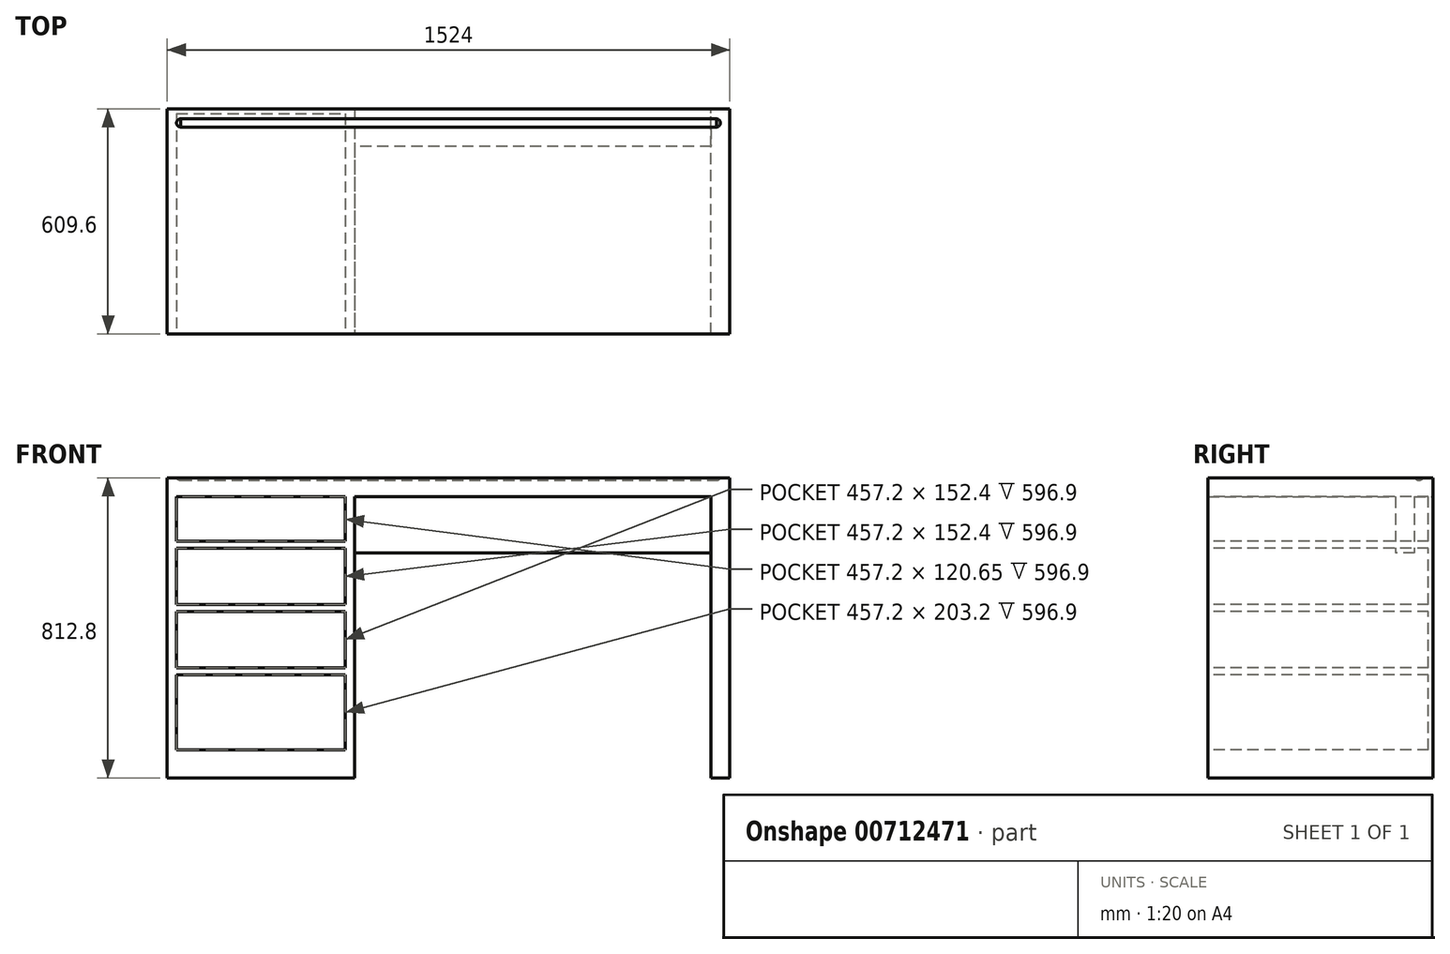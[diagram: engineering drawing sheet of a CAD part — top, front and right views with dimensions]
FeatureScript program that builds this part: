
annotation { "Feature Type Name" : "Feature", "Feature Type Description" : "" }
export const myFeature = defineFeature(function(context is Context, id is Id, definition is map)
    precondition{}
    {
        {
            var Q0;
            Q0=qCreatedBy(makeId("Top.planeOp"),FACE);
            var sketch = newSketch(context, id + "F0", { "sketchPlane" : qUnion([Q0])});
            skLineSegment(sketch, "E0.bottom", {"start": v(-762, 304.8) * mm, "end": v(762, 304.8) * mm});
            skLineSegment(sketch, "E0.top", {"start": v(-762, -304.8) * mm, "end": v(762, -304.8) * mm});
            skLineSegment(sketch, "E0.left", {"start": v(-762, 304.8) * mm, "end": v(-762, -304.8) * mm});
            skLineSegment(sketch, "E0.right", {"start": v(762, 304.8) * mm, "end": v(762, -304.8) * mm});
            skPoint(sketch, "E0.middle", {"position": v(0, 0) * mm});
            skSolve(sketch);
        }
        {
            var Q0;
            Q0 = qSketchRegion(id + "F0", true);
            extrude(context, id + "F1", {"entities" : qUnion([Q0]), "endBound" : BoundingType.SYMMETRIC, "depth" : 50.8 * mm, "offsetDistance" : 25.4 * mm});
        }
        {
            var Q0;
            Q0=makeQuery(id+"F1.opExtrude","CAP_FACE",FACE,{"disambiguationData":[OSD([sQuery(id+"F0.wireOp",EDGE,"E0.bottom"),sQuery(id+"F0.wireOp",EDGE,"E0.top"),sQuery(id+"F0.wireOp",EDGE,"E0.left"),sQuery(id+"F0.wireOp",EDGE,"E0.right")])],"isStart":true});
            var sketch = newSketch(context, id + "F2", { "sketchPlane" : qUnion([Q0])});
            skLineSegment(sketch, "E1.bottom", {"start": v(762, 304.8) * mm, "end": v(711.2, 304.8) * mm});
            skLineSegment(sketch, "E1.top", {"start": v(762, -304.8) * mm, "end": v(711.2, -304.8) * mm});
            skLineSegment(sketch, "E1.left", {"start": v(762, 304.8) * mm, "end": v(762, -304.8) * mm});
            skLineSegment(sketch, "E1.right", {"start": v(711.2, 304.8) * mm, "end": v(711.2, -304.8) * mm});
            skSolve(sketch);
        }
        {
            var Q0;
            Q0 = qSketchRegion(id + "F2", true);
            extrude(context, id + "F3", {"entities" : qUnion([Q0]), "operationType" : NewBodyOperationType.ADD, "depth" : 762 * mm, "offsetDistance" : 25.4 * mm});
        }
        {
            var Q0;
            Q0=makeQuery(id+"F1.opExtrude","CAP_FACE",FACE,{"disambiguationData":[OSD([sQuery(id+"F0.wireOp",EDGE,"E0.bottom"),sQuery(id+"F0.wireOp",EDGE,"E0.top"),sQuery(id+"F0.wireOp",EDGE,"E0.left"),sQuery(id+"F0.wireOp",EDGE,"E0.right")])],"isStart":true});
            var sketch = newSketch(context, id + "F4", { "sketchPlane" : qUnion([Q0])});
            skLineSegment(sketch, "E2.bottom", {"start": v(-762, -304.8) * mm, "end": v(-254, -304.8) * mm});
            skLineSegment(sketch, "E2.top", {"start": v(-762, 304.8) * mm, "end": v(-254, 304.8) * mm});
            skLineSegment(sketch, "E2.left", {"start": v(-762, -304.8) * mm, "end": v(-762, 304.8) * mm});
            skLineSegment(sketch, "E2.right", {"start": v(-254, -304.8) * mm, "end": v(-254, 304.8) * mm});
            skSolve(sketch);
        }
        {
            var Q0;
            Q0 = qSketchRegion(id + "F4", true);
            var Q1;
            Q1=makeQuery(id+"F3.opExtrude","CAP_FACE",FACE,{"disambiguationData":[OSD([sQuery(id+"F2.wireOp",EDGE,"E1.bottom"),sQuery(id+"F2.wireOp",EDGE,"E1.top"),sQuery(id+"F2.wireOp",EDGE,"E1.left"),sQuery(id+"F2.wireOp",EDGE,"E1.right")])],"isStart":false});
            extrude(context, id + "F5", {"entities" : qUnion([Q0]), "operationType" : NewBodyOperationType.ADD, "endBound" : BoundingType.UP_TO_SURFACE, "depth" : 721.36 * mm, "endBoundEntityFace" : qUnion([Q1]), "offsetDistance" : 25.4 * mm});
        }
        {
            var Q0;
            Q0=makeQuery(id+"F5.opExtrude","SWEPT_FACE",FACE,{"disambiguationData":[OSD([sQuery(id+"F4.wireOp",EDGE,"E2.right")])]});
            var sketch = newSketch(context, id + "F6", { "sketchPlane" : qUnion([Q0])});
            skLineSegment(sketch, "E3.bottom", {"start": v(254, -25.4) * mm, "end": v(203.2, -25.4) * mm});
            skLineSegment(sketch, "E3.top", {"start": v(254, -177.8) * mm, "end": v(203.2, -177.8) * mm});
            skLineSegment(sketch, "E3.left", {"start": v(254, -25.4) * mm, "end": v(254, -177.8) * mm});
            skLineSegment(sketch, "E3.right", {"start": v(203.2, -25.4) * mm, "end": v(203.2, -177.8) * mm});
            skSolve(sketch);
        }
        {
            var Q0;
            Q0 = qSketchRegion(id + "F6", true);
            extrude(context, id + "F7", {"entities" : qUnion([Q0]), "operationType" : NewBodyOperationType.ADD, "endBound" : BoundingType.UP_TO_NEXT, "depth" : 25.4 * mm, "offsetDistance" : 25.4 * mm});
        }
        {
            var Q0;
            Q0=makeQuery(id+"F5.boolean.opBoolean","MERGE",FACE,{"derivedFrom":[makeQuery(id+"F3.boolean.opBoolean","MERGE",FACE,{"derivedFrom":[makeQuery(id+"F1.opExtrude","SWEPT_FACE",FACE,{"disambiguationData":[OSD([sQuery(id+"F0.wireOp",EDGE,"E0.top")])]}),makeQuery(id+"F3.opExtrude","SWEPT_FACE",FACE,{"disambiguationData":[OSD([sQuery(id+"F2.wireOp",EDGE,"E1.bottom")])]})]}),makeQuery(id+"F5.opExtrude","SWEPT_FACE",FACE,{"disambiguationData":[OSD([sQuery(id+"F4.wireOp",EDGE,"E2.top")])]})]});
            var sketch = newSketch(context, id + "F8", { "sketchPlane" : qUnion([Q0])});
            skLineSegment(sketch, "E4", {"start": v(-508, -787.4) * mm, "end": v(-508, 25.4) * mm, "construction": true});
            skLineSegment(sketch, "E5.bottom", {"start": v(-736.6, -488.95) * mm, "end": v(-279.4, -488.95) * mm});
            skLineSegment(sketch, "E5.top", {"start": v(-736.6, -336.55) * mm, "end": v(-279.4, -336.55) * mm});
            skLineSegment(sketch, "E5.left", {"start": v(-736.6, -488.95) * mm, "end": v(-736.6, -336.55) * mm});
            skLineSegment(sketch, "E5.right", {"start": v(-279.4, -488.95) * mm, "end": v(-279.4, -336.55) * mm});
            skPoint(sketch, "E5.middle", {"position": v(-508, -412.75) * mm});
            skLineSegment(sketch, "E6.bottom", {"start": v(-736.6, -317.5) * mm, "end": v(-279.4, -317.5) * mm});
            skLineSegment(sketch, "E6.top", {"start": v(-736.6, -165.1) * mm, "end": v(-279.4, -165.1) * mm});
            skLineSegment(sketch, "E6.left", {"start": v(-736.6, -317.5) * mm, "end": v(-736.6, -165.1) * mm});
            skLineSegment(sketch, "E6.right", {"start": v(-279.4, -317.5) * mm, "end": v(-279.4, -165.1) * mm});
            skPoint(sketch, "E6.middle", {"position": v(-508, -241.3) * mm});
            skLineSegment(sketch, "E7.bottom", {"start": v(-736.6, -146.05) * mm, "end": v(-279.4, -146.05) * mm});
            skLineSegment(sketch, "E7.top", {"start": v(-736.6, -25.4) * mm, "end": v(-279.4, -25.4) * mm});
            skLineSegment(sketch, "E7.left", {"start": v(-736.6, -146.05) * mm, "end": v(-736.6, -25.4) * mm});
            skLineSegment(sketch, "E7.right", {"start": v(-279.4, -146.05) * mm, "end": v(-279.4, -25.4) * mm});
            skPoint(sketch, "E7.middle", {"position": v(-508, -85.72) * mm});
            skLineSegment(sketch, "E8.bottom", {"start": v(-736.6, -711.2) * mm, "end": v(-279.4, -711.2) * mm});
            skLineSegment(sketch, "E8.top", {"start": v(-736.6, -508) * mm, "end": v(-279.4, -508) * mm});
            skLineSegment(sketch, "E8.left", {"start": v(-736.6, -711.2) * mm, "end": v(-736.6, -508) * mm});
            skLineSegment(sketch, "E8.right", {"start": v(-279.4, -711.2) * mm, "end": v(-279.4, -508) * mm});
            skPoint(sketch, "E8.middle", {"position": v(-508, -609.6) * mm});
            skSolve(sketch);
        }
        {
            var Q0;
            Q0 = qSketchRegion(id + "F8", true);
            extrude(context, id + "F9", {"entities" : qUnion([Q0]), "operationType" : NewBodyOperationType.REMOVE, "oppositeDirection" : true, "depth" : 596.9 * mm, "offsetDistance" : 25.4 * mm});
        }
        {
            var Q0;
            Q0=qCreatedBy(makeId("Right.planeOp"),FACE);
            var sketch = newSketch(context, id + "F10", { "sketchPlane" : qUnion([Q0])});
            skCircle(sketch, "E9", {"center": v(266.7, 31.75) * mm, "radius": 12.7 * mm});
            skSolve(sketch);
        }
        {
            var Q0;
            Q0 = qSketchRegion(id + "F10", true);
            extrude(context, id + "F11", {"entities" : qUnion([Q0]), "operationType" : NewBodyOperationType.REMOVE, "endBound" : BoundingType.SYMMETRIC, "oppositeDirection" : true, "depth" : 1473.2 * mm, "offsetDistance" : 25.4 * mm});
        }
        {
            var Q0;
            Q0=makeQuery(id+"F11.boolean.opBoolean","COPY",EDGE,{"derivedFrom":makeQuery(id+"F11.opExtrude","CAP_EDGE",EDGE,{"disambiguationData":[OSD([sQuery(id+"F10.wireOp",EDGE,"E9")])],"isStart":false})});
            var Q1;
            Q1=makeQuery(id+"F11.boolean.opBoolean","COPY",EDGE,{"derivedFrom":makeQuery(id+"F11.opExtrude","CAP_EDGE",EDGE,{"disambiguationData":[OSD([sQuery(id+"F10.wireOp",EDGE,"E9")])],"isStart":true})});
            fillet(context, id + "F12", {"entities" : qUnion([Q0, Q1]), "radius" : 12.7 * mm, "tangentPropagation" : true, "allowEdgeOverflow" : false});
        }
    });
